FCSTD DOCUMENT  (FreeCAD 1.1R38827 (Git))
Label: composit_stand3_bar_decor_main
License: All rights reserved
LicenseURL: http://en.wikipedia.org/wiki/All_rights_reserved
objects: Sketcher::SketchObject×1
note: 2 computed .brp shape members not serialized (recipe doc carries the construction recipe); baked Part::Feature solids carry a one-line shape summary decoded from their .brp
EXTERNAL_REF file=composit_stand3_bar_main.FCStd obj=Spreadsheet
EXTERNAL_REF file=composit_stand3_plexiglass_outer_main.FCStd obj=Spreadsheet

FEATURE [Sketcher::SketchObject] Sketch
  ArcFitTolerance = 0
  FullyConstrained = true
  MakeInternals = false
  expr: Constraints[2] = <<composit_stand3_bar_main>>#<<Properties>>.length + <<composit_stand3_plexiglass_outer_main>>#<<Properties>>.thickness
  expr: Constraints[4] = <<composit_stand3_bar_main>>#<<Properties>>.width
  sketch-geometry (2):
    g0: LineSegment StartX=-9e-16 StartY=-18.3 StartZ=0 EndX=0 EndY=18.3 EndZ=0
    g1: LineSegment StartX=0 StartY=18.3 StartZ=0 EndX=20.5 EndY=18.3 EndZ=0
  constraints (6):
    c: Coincident(g0,g1)
    c: Horizontal(g1)
    c: DistanceX(g1) = 20.5
    c: Symmetric(g0,g0,g-1)
    c: DistanceY(g0,g0) = 36.6
    c: PointOnObject(g0,g-2)
